# Revit family: NBS_Senator_OffcChrs_Jonny_JNY01
name_source: partatom
category: Furniture
revit_build: Autodesk Revit 2016 (Build: 20151007_0715(x64)
units: mm (PartAtom-declared; Revit-internal decimal feet)

## family parameters
Always vertical = Yes
Cut with Voids When Loaded = No
Room Calculation Point = No
Shared = No
Work Plane-Based = No

## types (4) — shared parameters
AssetType = Moveable
Category = Pr_40_50_12_57:Office chairs
CodePerformance = BS EN 16139: 2013-L1
Description = Plastic seat and back
DurationUnit = year
FrameColourOptions = Silver, black
FrameFinish = Powder coat
FrameMaterials = Steel
FrameMountingMaterial = NBS_Concept
IfcExportAs = IfcFurnitureType
IfcExportType = CHAIR
IsBuiltIn = No
ManufacturerName = Senator
ManufacturerURL = www.senator.co.uk
Material = Steel
ModelReference = Jonny chair
NBSCertification = www.nationalbimlibrary.com/cert/huzy5xz5
NBSDescription = Office chairs
NBSReference = 45-35-20/330
NominalDepth = 610 mm  [stored 2.00131 ft]
NominalHeight = 835 mm
NominalLength = 560 mm  [stored 1.83727 ft]
OptionalFeatures = Tubular steel frame available in black powder coat, plastic glides available in black or graphite, plastic arms available in black or graphite
ProductInformation = www.thesenatorgroup.com/FamilyDocuments/768/SENATOR%20Spec%20Sheet%20-%20Jonny.pdf
SeatArmMaterial = NBS_Concept
SeatFrameMaterial = NBS_Concept
SeatMaterial = NBS_Concept
SeatingHeight = 460 mm  [stored 1.50919 ft]
SeatingSeatBackMaterial = NBS_Concept
SeatingSeatMaterial = NBS_Concept
SeatsAndBacksColourOptions = Black, light grey, graphite, turtle dove, storm,  vintage red, orange crush, citrus, azure blue or aqua
SeatsAndBacksMaterial = Plastic
Size = 560 x 610 x 835 mm
StandardsDimensions = BS EN 16139: 2013 Level 1
StandardsDurability = BS EN 16139: 2013 Level 1
StandardsSafetyRequirements = BS EN 16139: 2013 Level 1
Status = UNSET
SustainabilityPerformance = 100% recycleable
Uniclass2015Code = Pr_40_50_12_57
Uniclass2015Title = Office chairs
Uniclass2015Version = Products v1.9
Version = 1
WarrantyDescription = Senator warrants that its manufactured products are free from defects for a period of ten years on Senator seating ranges
WarrantyDurationParts = 10
WarrantyDurationUnit = year
zero-valued in all types: HighestSeatingHeight, LowestSeatingHeight

## per-type parameters (varying)
| type | BIMObjectName | HasArms | HasCastors | HasGlides | ModelNumber | Name |
| JNY01A | NBS_Senator_OfficeChairs_Jonny_JNY01A | Yes | No | Yes | JNY01A | OfficeChairs_Jonny_JNY01A_Senator |
| JNY01 | NBS_Senator_OfficeChairs_Jonny_JNY01 | No | No | Yes | JNY01 | OfficeChairs_Jonny_JNY01_Senator |
| JNY03 | NBS_Senator_OfficeChairs_Jonny_JNY03 | No | Yes | No | JNY03 | OfficeChairs_Jonny_JNY03_Senator |
| JNY03A | NBS_Senator_OfficeChairs_Jonny_JNY03A | Yes | Yes | No | JNY03 | OfficeChairs_Jonny_JNY03_Senator |

note: [stored X ft] marks values corroborated as IEEE doubles in the binary element streams (Revit-internal decimal feet)

## geometry (parser evidence)
native form markers: Sweep x12
no freeform markers — native parametric forms only
